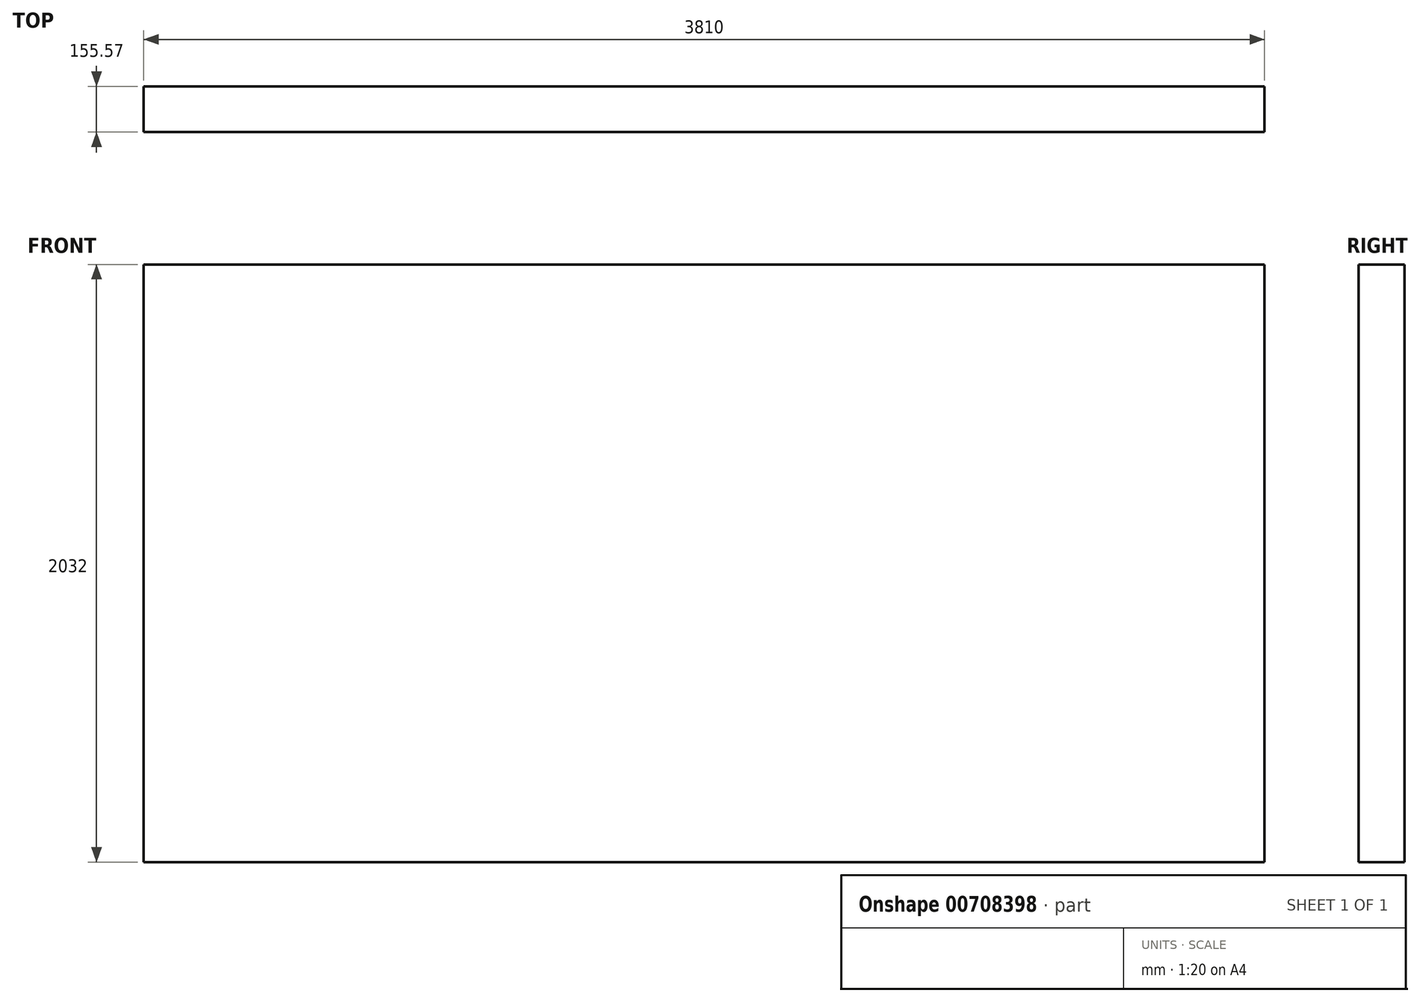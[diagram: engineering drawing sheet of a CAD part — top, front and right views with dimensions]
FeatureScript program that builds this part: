
annotation { "Feature Type Name" : "Feature", "Feature Type Description" : "" }
export const myFeature = defineFeature(function(context is Context, id is Id, definition is map)
    precondition{}
    {
        {
            var Q0;
            Q0=qCreatedBy(makeId("Front.planeOp"),FACE);
            var sketch = newSketch(context, id + "F0", { "sketchPlane" : qUnion([Q0])});
            skLineSegment(sketch, "E0.bottom", {"start": v(0, -151.3) * mm, "end": v(3810, -151.3) * mm});
            skLineSegment(sketch, "E0.top", {"start": v(0, 1880.7) * mm, "end": v(3810, 1880.7) * mm});
            skLineSegment(sketch, "E0.left", {"start": v(0, -151.3) * mm, "end": v(0, 1880.7) * mm});
            skLineSegment(sketch, "E0.right", {"start": v(3810, -151.3) * mm, "end": v(3810, 1880.7) * mm});
            skSolve(sketch);
        }
        {
            var Q0;
            Q0=makeQuery(id+"F0.imprint","IMPRINT",FACE,{"disambiguationData":[TD([[makeQuery(id+"F0.imprint","IMPRINT",EDGE,{"derivedFrom":sQuery(id+"F0.wireOp",EDGE,"E0.bottom")}),1.0]])]});
            extrude(context, id + "F1", {"entities" : qUnion([Q0]), "oppositeDirection" : true, "depth" : 155.57 * mm, "offsetDistance" : 25.4 * mm});
        }
    });
